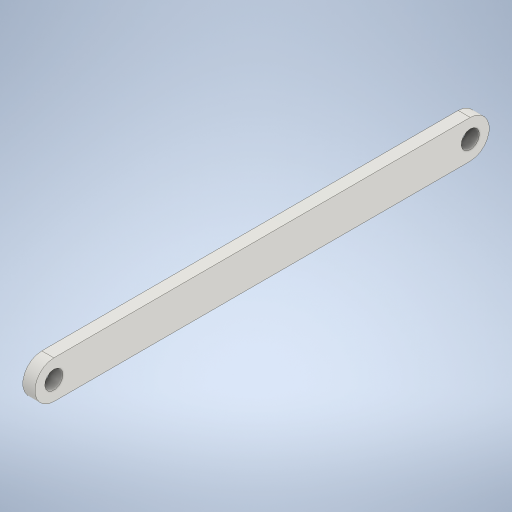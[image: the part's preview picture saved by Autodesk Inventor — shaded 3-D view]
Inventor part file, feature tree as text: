
AUTODESK INVENTOR PART (.ipt)
format: ipt  version: 2024 (Build 280153000, 153)  size: 357,376 bytes
history: native  units: mm
features: other x2, extrude x1, sketch x1
ambient origin geometry x8: Origin, YZ Plane, XZ Plane, XY Plane, X Axis, Y Axis, Z Axis, Center Point
bodies: Solid1 (feature_tree)
feature tree (4):
  extrude  "Extrusion1"  Depth=25.0mm
  other  "Full Round Fillet1"
  other  "Full Round Fillet2"
  sketch  "Sketch1"  dims[d0=300.0mm d1=25.0mm d2=12.5mm d3=150.0mm d4=12.0mm d5=12.5mm d6=12.0mm d7=12.5mm d8=8.0mm d9=0.0mm]
